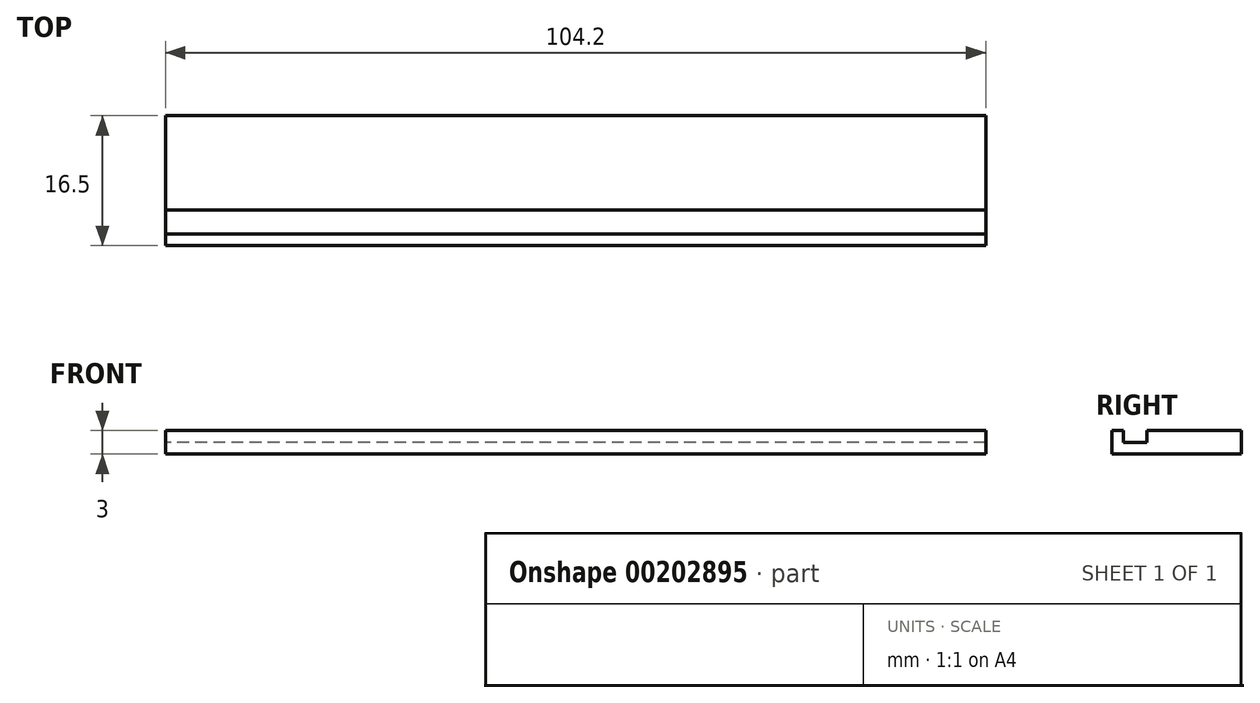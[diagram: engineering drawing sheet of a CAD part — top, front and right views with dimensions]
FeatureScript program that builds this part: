
annotation { "Feature Type Name" : "Feature", "Feature Type Description" : "" }
export const myFeature = defineFeature(function(context is Context, id is Id, definition is map)
    precondition{}
    {
        {
            var Q0;
            Q0=qCreatedBy(makeId("Right.planeOp"),FACE);
            var sketch = newSketch(context, id + "F0", { "sketchPlane" : qUnion([Q0])});
            skLineSegment(sketch, "E0", {"start": v(-4.63, 0) * mm, "end": v(7.64, 0) * mm, "construction": true});
            skLineSegment(sketch, "E1", {"start": v(0, 6.92) * mm, "end": v(0, -6.64) * mm, "construction": true});
            skLineSegment(sketch, "E2", {"start": v(-3, 3) * mm, "end": v(-3, 0) * mm});
            skLineSegment(sketch, "E3", {"start": v(-3, 0) * mm, "end": v(0, 0) * mm});
            skLineSegment(sketch, "E4", {"start": v(-3, 3) * mm, "end": v(-1.5, 3) * mm});
            skLineSegment(sketch, "E5", {"start": v(-1.5, 3) * mm, "end": v(-1.5, 1.5) * mm});
            skLineSegment(sketch, "E6", {"start": v(-1.5, 1.5) * mm, "end": v(0, 1.5) * mm});
            skLineSegment(sketch, "E7.MirrorCS", {"start": v(1.5, 3) * mm, "end": v(1.5, 1.5) * mm});
            skLineSegment(sketch, "E8.MirrorCS", {"start": v(1.5, 1.5) * mm, "end": v(0, 1.5) * mm});
            skLineSegment(sketch, "E9.MirrorCS", {"start": v(3, 3) * mm, "end": v(1.5, 3) * mm});
            skLineSegment(sketch, "E10.MirrorCS", {"start": v(3, 0) * mm, "end": v(0, 0) * mm});
            skLineSegment(sketch, "E11", {"start": v(3, 0) * mm, "end": v(13.5, 0) * mm});
            skLineSegment(sketch, "E12", {"start": v(13.5, 0) * mm, "end": v(13.5, 3) * mm});
            skLineSegment(sketch, "E13", {"start": v(13.5, 3) * mm, "end": v(3, 3) * mm});
            skSolve(sketch);
        }
        {
            var Q0;
            Q0=qSketchRegion(id+"F0",true);
            extrude(context, id + "F1", {"entities" : qUnion([Q0]), "depth" : 104.2 * mm});
        }
    });
